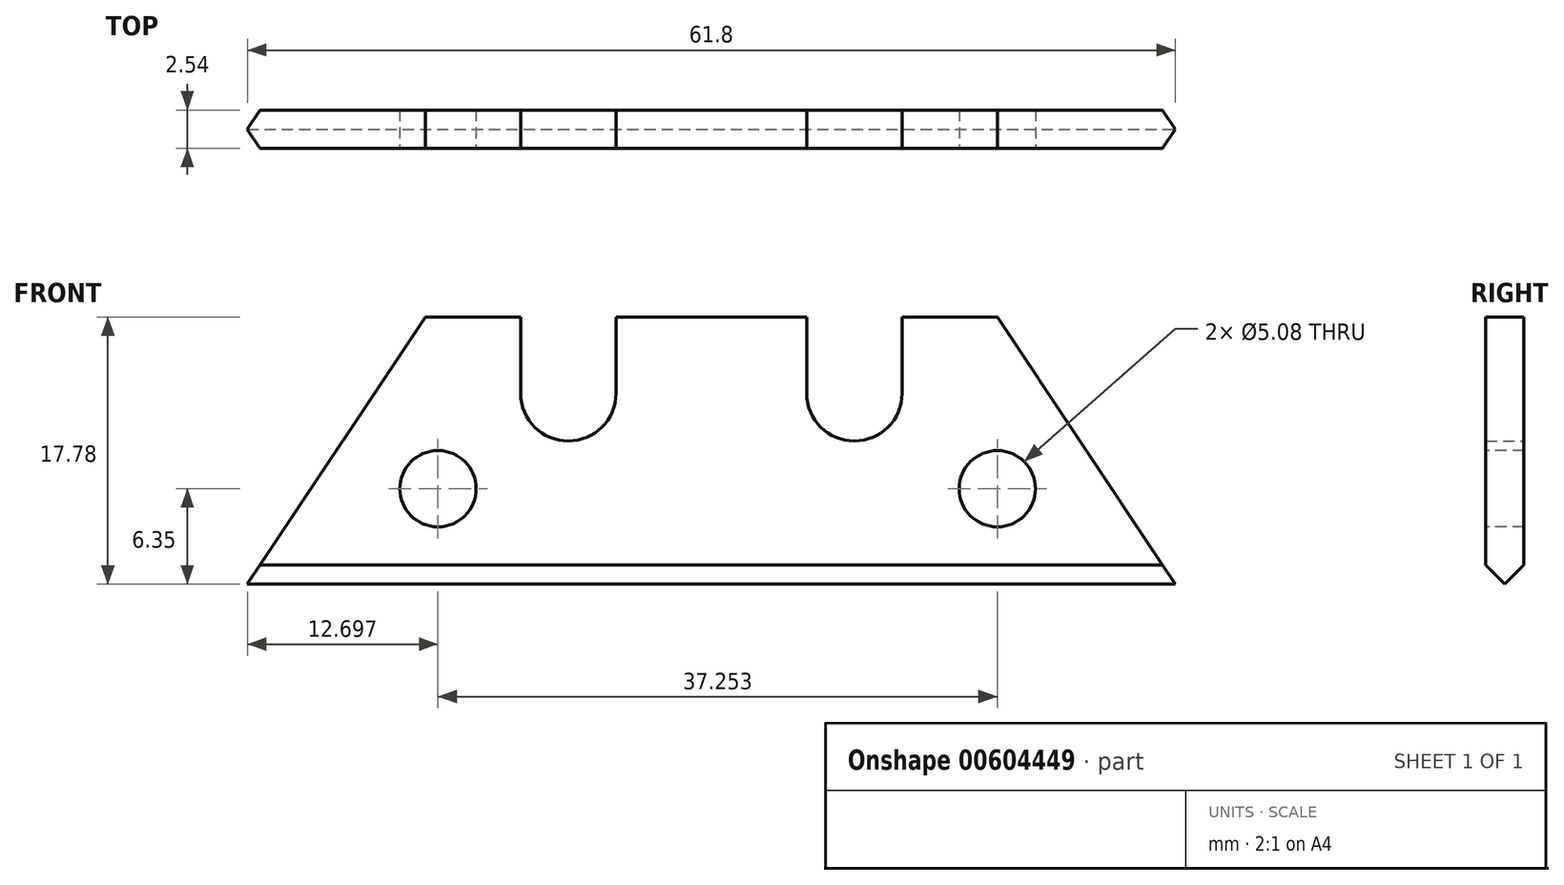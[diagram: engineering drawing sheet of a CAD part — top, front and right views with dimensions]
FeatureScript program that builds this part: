
annotation { "Feature Type Name" : "Feature", "Feature Type Description" : "" }
export const myFeature = defineFeature(function(context is Context, id is Id, definition is map)
    precondition{}
    {
        {
            var Q0;
            Q0=qCreatedBy(makeId("Front.planeOp"),FACE);
            var sketch = newSketch(context, id + "F0", { "sketchPlane" : qUnion([Q0])});
            skLineSegment(sketch, "E0", {"start": v(0, 0) * mm, "end": v(-63.5, 0) * mm});
            skLineSegment(sketch, "E1", {"start": v(-63.5, 0) * mm, "end": v(-50.8, 19.05) * mm});
            skLineSegment(sketch, "E2", {"start": v(-50.8, 19.05) * mm, "end": v(-44.45, 19.05) * mm});
            skLineSegment(sketch, "E3", {"start": v(-44.45, 19.05) * mm, "end": v(-44.45, 13.97) * mm});
            skLineSegment(sketch, "E4", {"start": v(-38.1, 13.97) * mm, "end": v(-38.1, 19.05) * mm});
            skLineSegment(sketch, "E5", {"start": v(-38.1, 19.05) * mm, "end": v(-25.4, 19.05) * mm});
            skLineSegment(sketch, "E6", {"start": v(-25.4, 19.05) * mm, "end": v(-25.4, 13.97) * mm});
            skLineSegment(sketch, "E7", {"start": v(-19.05, 13.97) * mm, "end": v(-19.05, 19.05) * mm});
            skLineSegment(sketch, "E8", {"start": v(-19.05, 19.05) * mm, "end": v(-12.7, 19.05) * mm});
            skLineSegment(sketch, "E9", {"start": v(-12.7, 19.05) * mm, "end": v(0, 0) * mm});
            skArc(sketch, "E10", {"start": v(-44.45, 13.97) * mm, "mid": v(-41.27, 10.8) * mm, "end": v(-38.1, 13.97) * mm});
            skArc(sketch, "E11", {"start": v(-25.4, 13.97) * mm, "mid": v(-22.22, 10.8) * mm, "end": v(-19.05, 13.97) * mm});
            skSolve(sketch);
        }
        {
            var Q0;
            Q0 = qSketchRegion(id + "F0", true);
            extrude(context, id + "F1", {"entities" : qUnion([Q0]), "depth" : 2.54 * mm, "offsetDistance" : 25.4 * mm});
        }
        {
            var Q0;
            Q0=makeQuery(id+"F1.opExtrude","CAP_EDGE",EDGE,{"disambiguationData":[OSD([sQuery(id+"F0.wireOp",EDGE,"E0")])],"isStart":false});
            var Q1;
            Q1=makeQuery(id+"F1.opExtrude","CAP_EDGE",EDGE,{"disambiguationData":[OSD([sQuery(id+"F0.wireOp",EDGE,"E0")])],"isStart":true});
            chamfer(context, id + "F2", {"entities" : qUnion([Q0, Q1]), "width" : 2.54 * mm, "tangentPropagation" : true});
        }
        {
            var Q0;
            Q0=makeQuery(id+"F1.opExtrude","CAP_FACE",FACE,{"disambiguationData":[OSD([sQuery(id+"F0.wireOp",EDGE,"E0"),sQuery(id+"F0.wireOp",EDGE,"E1"),sQuery(id+"F0.wireOp",EDGE,"E2"),sQuery(id+"F0.wireOp",EDGE,"E3"),sQuery(id+"F0.wireOp",EDGE,"E4"),sQuery(id+"F0.wireOp",EDGE,"E5"),sQuery(id+"F0.wireOp",EDGE,"E6"),sQuery(id+"F0.wireOp",EDGE,"E7"),sQuery(id+"F0.wireOp",EDGE,"E8"),sQuery(id+"F0.wireOp",EDGE,"E9"),sQuery(id+"F0.wireOp",EDGE,"E10"),sQuery(id+"F0.wireOp",EDGE,"E11")])],"isStart":false});
            var sketch = newSketch(context, id + "F3", { "sketchPlane" : qUnion([Q0])});
            skCircle(sketch, "E12", {"center": v(-12.7, 7.62) * mm, "radius": 2.54 * mm});
            skCircle(sketch, "E13", {"center": v(-49.95, 7.62) * mm, "radius": 2.54 * mm});
            skSolve(sketch);
        }
        {
            var Q0;
            Q0 = qSketchRegion(id + "F3", true);
            extrude(context, id + "F4", {"entities" : qUnion([Q0]), "operationType" : NewBodyOperationType.REMOVE, "oppositeDirection" : true, "depth" : 2.54 * mm, "offsetDistance" : 25.4 * mm});
        }
    });
